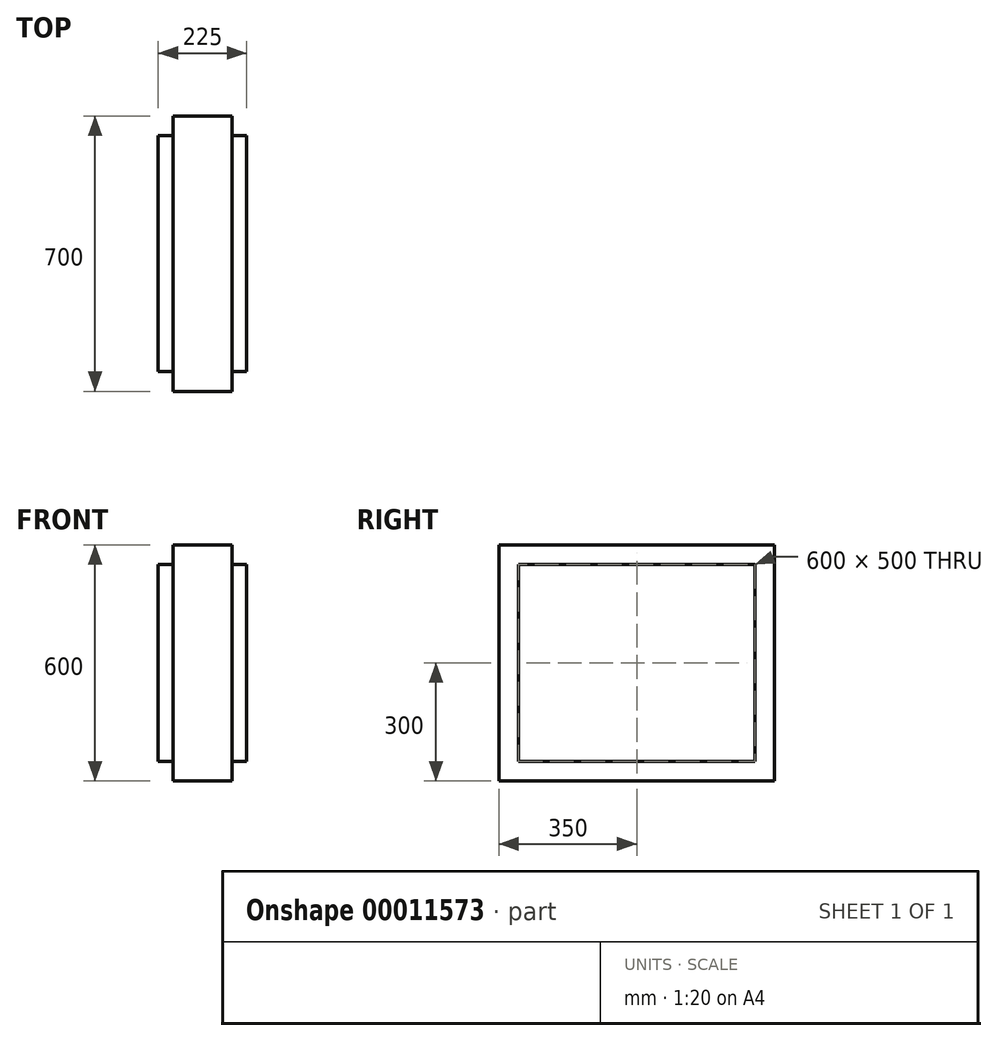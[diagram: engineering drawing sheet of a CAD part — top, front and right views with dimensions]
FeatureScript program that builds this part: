
annotation { "Feature Type Name" : "Feature", "Feature Type Description" : "" }
export const myFeature = defineFeature(function(context is Context, id is Id, definition is map)
    precondition{}
    {
        {
            var Q0;
            Q0=qCreatedBy(makeId("Right.planeOp"),FACE);
            var sketch = newSketch(context, id + "F0", { "sketchPlane" : qUnion([Q0])});
            skLineSegment(sketch, "E0.rect.bottom", {"start": v(-300, 250) * mm, "end": v(300, 250) * mm});
            skLineSegment(sketch, "E0.rect.top", {"start": v(-300, -250) * mm, "end": v(300, -250) * mm});
            skLineSegment(sketch, "E0.rect.left", {"start": v(-300, 250) * mm, "end": v(-300, -250) * mm});
            skLineSegment(sketch, "E0.rect.right", {"start": v(300, 250) * mm, "end": v(300, -250) * mm});
            skPoint(sketch, "E0.rect.middle", {"position": v(0, 0) * mm});
            skSolve(sketch);
        }
        {
            var Q0;
            Q0=makeQuery(id+"F0.imprint","IMPRINT",FACE,{"disambiguationData":[TD([[makeQuery(id+"F0.imprint","IMPRINT",EDGE,{"derivedFrom":sQuery(id+"F0.wireOp",EDGE,"E0.rect.bottom")}),-1.0]])]});
            extrude(context, id + "F1", {"entities" : qUnion([Q0]), "endBound" : BoundingType.SYMMETRIC, "depth" : 225 * mm});
        }
        {
            var Q0;
            Q0=qCreatedBy(makeId("Right.planeOp"),FACE);
            var sketch = newSketch(context, id + "F2", { "sketchPlane" : qUnion([Q0])});
            skLineSegment(sketch, "E1.rect.bottom", {"start": v(-350, 300) * mm, "end": v(350, 300) * mm});
            skLineSegment(sketch, "E1.rect.top", {"start": v(-350, -300) * mm, "end": v(350, -300) * mm});
            skLineSegment(sketch, "E1.rect.left", {"start": v(-350, 300) * mm, "end": v(-350, -300) * mm});
            skLineSegment(sketch, "E1.rect.right", {"start": v(350, 300) * mm, "end": v(350, -300) * mm});
            skPoint(sketch, "E1.rect.middle", {"position": v(0, 0) * mm});
            skSolve(sketch);
        }
        {
            var Q0;
            Q0 = qSketchRegion(id + "F2", true);
            extrude(context, id + "F3", {"entities" : qUnion([Q0]), "operationType" : NewBodyOperationType.ADD, "endBound" : BoundingType.SYMMETRIC, "depth" : 150 * mm});
        }
    });
